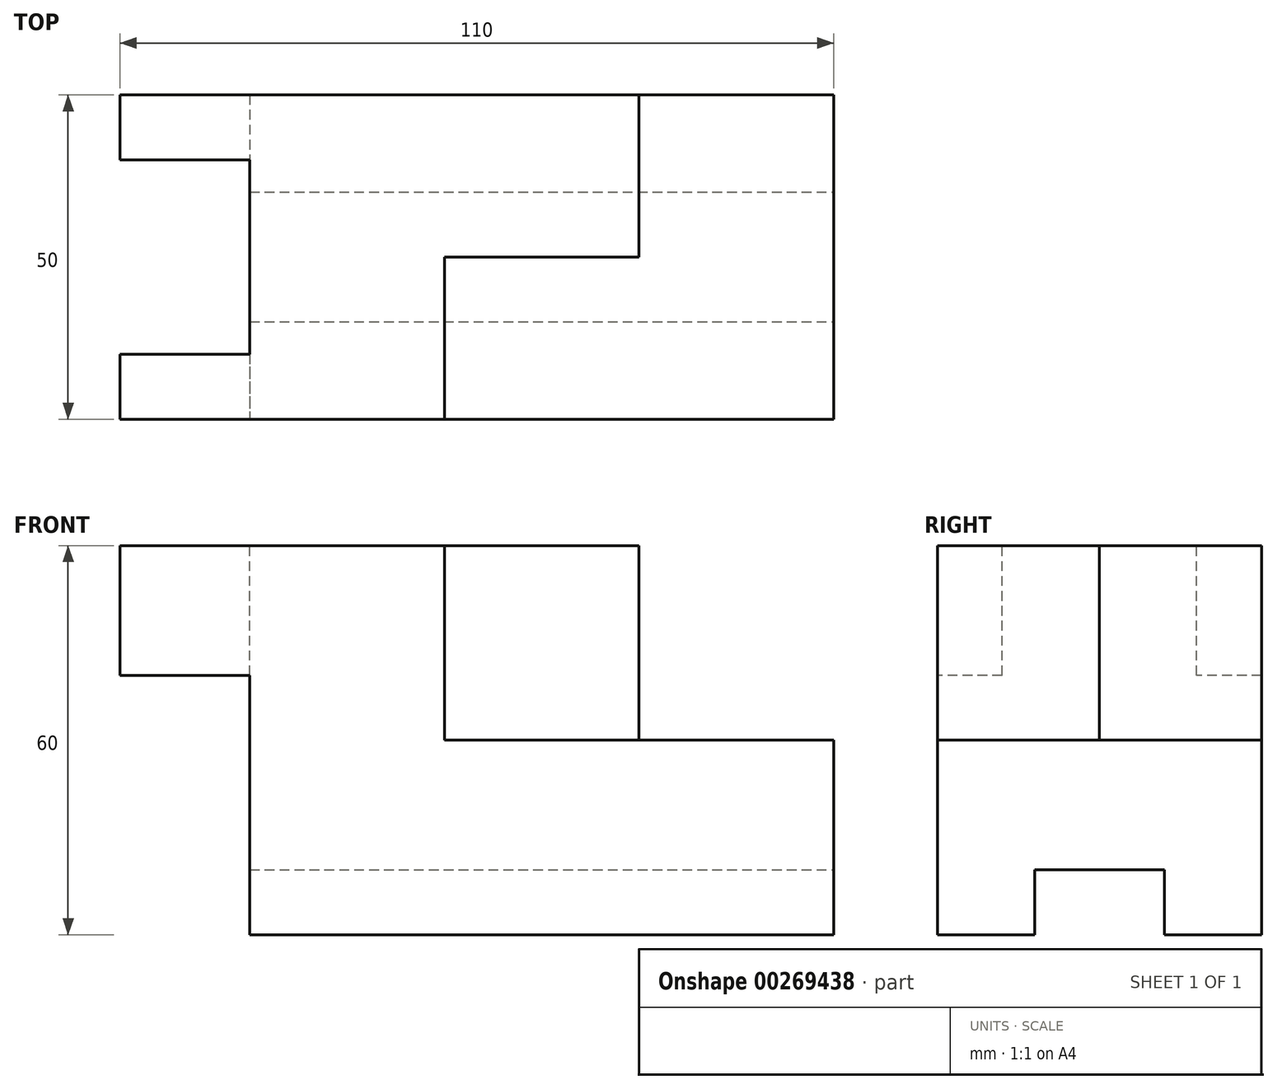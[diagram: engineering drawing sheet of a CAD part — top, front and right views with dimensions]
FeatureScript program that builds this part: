
annotation { "Feature Type Name" : "Feature", "Feature Type Description" : "" }
export const myFeature = defineFeature(function(context is Context, id is Id, definition is map)
    precondition{}
    {
        {
            var Q0;
            Q0=qCreatedBy(makeId("Top.planeOp"),FACE);
            var sketch = newSketch(context, id + "F0", { "sketchPlane" : qUnion([Q0])});
            skLineSegment(sketch, "E0.bottom", {"start": v(-55, 25) * mm, "end": v(55, 25) * mm});
            skLineSegment(sketch, "E0.top", {"start": v(-55, -25) * mm, "end": v(55, -25) * mm});
            skLineSegment(sketch, "E0.left", {"start": v(-55, 25) * mm, "end": v(-55, -25) * mm});
            skLineSegment(sketch, "E0.right", {"start": v(55, 25) * mm, "end": v(55, -25) * mm});
            skPoint(sketch, "E0.middle", {"position": v(0, 0) * mm});
            skSolve(sketch);
        }
        {
            var Q0;
            Q0 = qSketchRegion(id + "F0", true);
            extrude(context, id + "F1", {"entities" : qUnion([Q0]), "depth" : 60 * mm});
        }
        {
            var Q0;
            Q0=makeQuery(id+"F1.opExtrude","SWEPT_FACE",FACE,{"disambiguationData":[OSD([sQuery(id+"F0.wireOp",EDGE,"E0.top")])]});
            var sketch = newSketch(context, id + "F2", { "sketchPlane" : qUnion([Q0])});
            skLineSegment(sketch, "E1.bottom", {"start": v(55, 60) * mm, "end": v(25, 60) * mm});
            skLineSegment(sketch, "E1.top", {"start": v(55, 30) * mm, "end": v(25, 30) * mm});
            skLineSegment(sketch, "E1.left", {"start": v(55, 60) * mm, "end": v(55, 30) * mm});
            skLineSegment(sketch, "E1.right", {"start": v(25, 60) * mm, "end": v(25, 30) * mm});
            skSolve(sketch);
        }
        {
            var Q0;
            Q0 = qSketchRegion(id + "F2", true);
            extrude(context, id + "F3", {"entities" : qUnion([Q0]), "operationType" : NewBodyOperationType.REMOVE, "endBound" : BoundingType.THROUGH_ALL, "oppositeDirection" : true, "depth" : 25 * mm});
        }
        {
            var Q0;
            Q0=makeQuery(id+"F1.opExtrude","SWEPT_FACE",FACE,{"disambiguationData":[OSD([sQuery(id+"F0.wireOp",EDGE,"E0.top")])]});
            var sketch = newSketch(context, id + "F4", { "sketchPlane" : qUnion([Q0])});
            skLineSegment(sketch, "E2.bottom", {"start": v(-55, 0) * mm, "end": v(-35, 0) * mm});
            skLineSegment(sketch, "E2.top", {"start": v(-55, 40) * mm, "end": v(-35, 40) * mm});
            skLineSegment(sketch, "E2.left", {"start": v(-55, 0) * mm, "end": v(-55, 40) * mm});
            skLineSegment(sketch, "E2.right", {"start": v(-35, 0) * mm, "end": v(-35, 40) * mm});
            skSolve(sketch);
        }
        {
            var Q0;
            Q0 = qSketchRegion(id + "F4", true);
            extrude(context, id + "F5", {"entities" : qUnion([Q0]), "operationType" : NewBodyOperationType.REMOVE, "endBound" : BoundingType.THROUGH_ALL, "oppositeDirection" : true, "depth" : 25 * mm});
        }
        {
            var Q0;
            Q0=makeQuery(id+"F1.opExtrude","SWEPT_FACE",FACE,{"disambiguationData":[OSD([sQuery(id+"F0.wireOp",EDGE,"E0.top")])]});
            var sketch = newSketch(context, id + "F6", { "sketchPlane" : qUnion([Q0])});
            skLineSegment(sketch, "E3.bottom", {"start": v(25, 60) * mm, "end": v(-5, 60) * mm});
            skLineSegment(sketch, "E3.top", {"start": v(25, 30) * mm, "end": v(-5, 30) * mm});
            skLineSegment(sketch, "E3.left", {"start": v(25, 60) * mm, "end": v(25, 30) * mm});
            skLineSegment(sketch, "E3.right", {"start": v(-5, 60) * mm, "end": v(-5, 30) * mm});
            skSolve(sketch);
        }
        {
            var Q0;
            Q0 = qSketchRegion(id + "F6", true);
            extrude(context, id + "F7", {"entities" : qUnion([Q0]), "operationType" : NewBodyOperationType.REMOVE, "oppositeDirection" : true, "depth" : 25 * mm});
        }
        {
            var Q0;
            Q0=makeQuery(id+"F1.opExtrude","SWEPT_FACE",FACE,{"disambiguationData":[OSD([sQuery(id+"F0.wireOp",EDGE,"E0.right")])]});
            var sketch = newSketch(context, id + "F8", { "sketchPlane" : qUnion([Q0])});
            skLineSegment(sketch, "E4.bottom", {"start": v(-10, 0) * mm, "end": v(10, 0) * mm});
            skLineSegment(sketch, "E4.top", {"start": v(-10, 10) * mm, "end": v(10, 10) * mm});
            skLineSegment(sketch, "E4.left", {"start": v(-10, 0) * mm, "end": v(-10, 10) * mm});
            skLineSegment(sketch, "E4.right", {"start": v(10, 0) * mm, "end": v(10, 10) * mm});
            skSolve(sketch);
        }
        {
            var Q0;
            Q0 = qSketchRegion(id + "F8", true);
            extrude(context, id + "F9", {"entities" : qUnion([Q0]), "operationType" : NewBodyOperationType.REMOVE, "endBound" : BoundingType.THROUGH_ALL, "oppositeDirection" : true, "depth" : 25 * mm});
        }
        {
            var Q0;
            Q0=makeQuery(id+"F1.opExtrude","CAP_FACE",FACE,{"disambiguationData":[OSD([sQuery(id+"F0.wireOp",EDGE,"E0.bottom"),sQuery(id+"F0.wireOp",EDGE,"E0.top"),sQuery(id+"F0.wireOp",EDGE,"E0.left"),sQuery(id+"F0.wireOp",EDGE,"E0.right")])],"isStart":false});
            var sketch = newSketch(context, id + "F10", { "sketchPlane" : qUnion([Q0])});
            skLineSegment(sketch, "E5.bottom", {"start": v(-55, 15) * mm, "end": v(-35, 15) * mm});
            skLineSegment(sketch, "E5.top", {"start": v(-55, -15) * mm, "end": v(-35, -15) * mm});
            skLineSegment(sketch, "E5.left", {"start": v(-55, 15) * mm, "end": v(-55, -15) * mm});
            skLineSegment(sketch, "E5.right", {"start": v(-35, 15) * mm, "end": v(-35, -15) * mm});
            skSolve(sketch);
        }
        {
            var Q0;
            Q0 = qSketchRegion(id + "F10", true);
            extrude(context, id + "F11", {"entities" : qUnion([Q0]), "operationType" : NewBodyOperationType.REMOVE, "endBound" : BoundingType.THROUGH_ALL, "oppositeDirection" : true, "depth" : 25 * mm});
        }
    });
